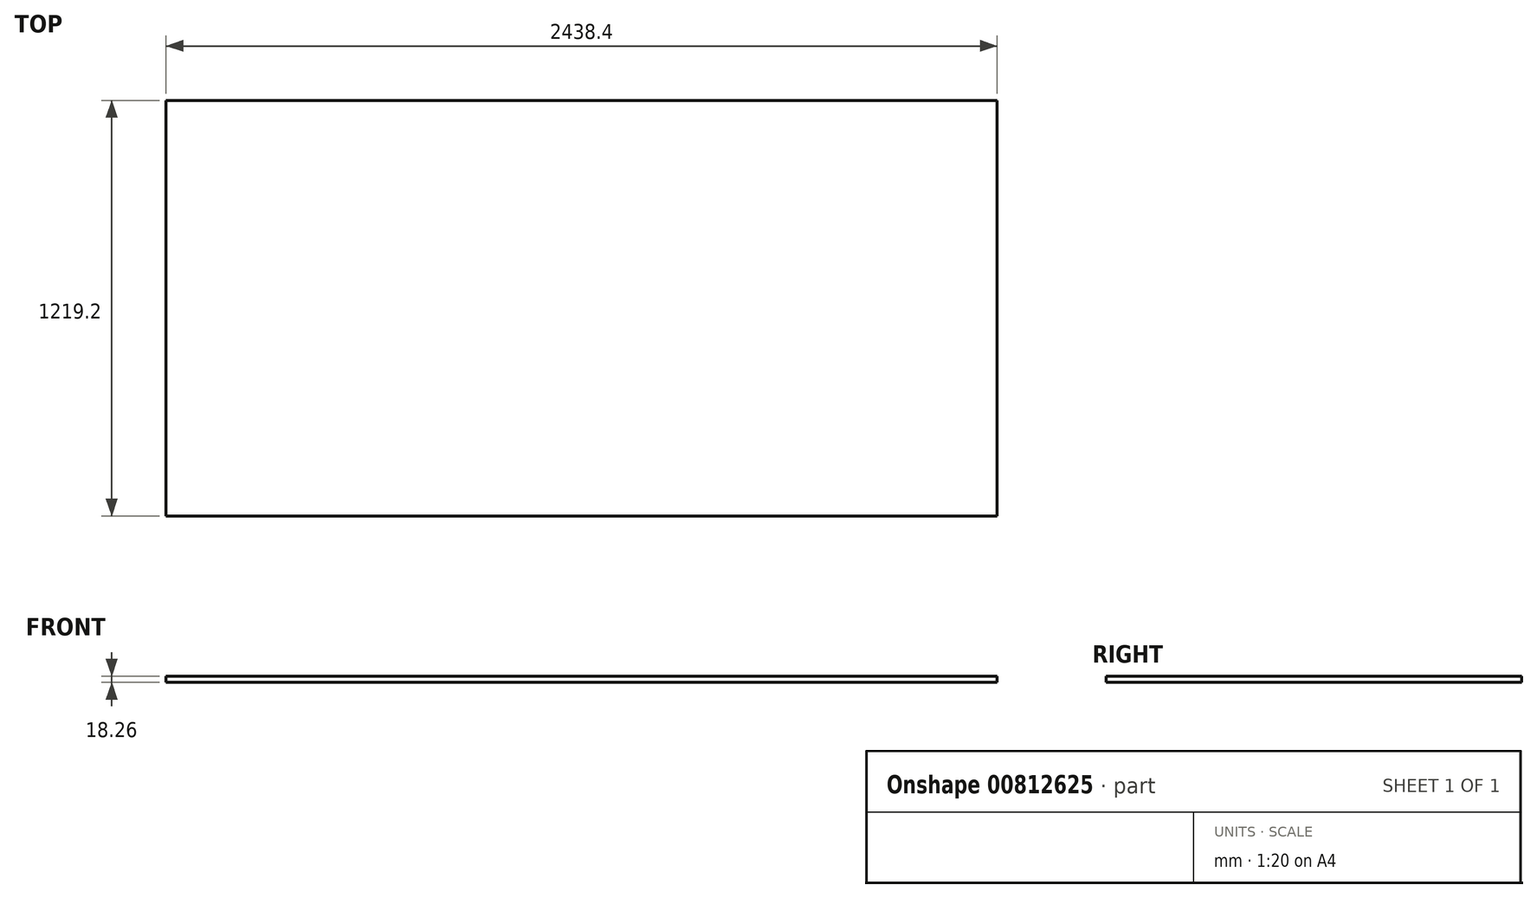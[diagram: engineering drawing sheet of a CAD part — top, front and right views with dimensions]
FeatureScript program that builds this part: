
annotation { "Feature Type Name" : "Feature", "Feature Type Description" : "" }
export const myFeature = defineFeature(function(context is Context, id is Id, definition is map)
    precondition{}
    {
        {
            var Q0;
            Q0=qCreatedBy(makeId("Top.planeOp"),FACE);
            var sketch = newSketch(context, id + "F0", { "sketchPlane" : qUnion([Q0])});
            skLineSegment(sketch, "E0.bottom", {"start": v(1219.2, 609.6) * mm, "end": v(-1219.2, 609.6) * mm});
            skLineSegment(sketch, "E0.top", {"start": v(1219.2, -609.6) * mm, "end": v(-1219.2, -609.6) * mm});
            skLineSegment(sketch, "E0.left", {"start": v(1219.2, 609.6) * mm, "end": v(1219.2, -609.6) * mm});
            skLineSegment(sketch, "E0.right", {"start": v(-1219.2, 609.6) * mm, "end": v(-1219.2, -609.6) * mm});
            skPoint(sketch, "E0.middle", {"position": v(0, 0) * mm});
            skSolve(sketch);
        }
        {
            var Q0;
            Q0 = qSketchRegion(id + "F0", true);
            extrude(context, id + "F1", {"entities" : qUnion([Q0]), "depth" : 18.26 * mm, "offsetDistance" : 25.4 * mm});
        }
    });
